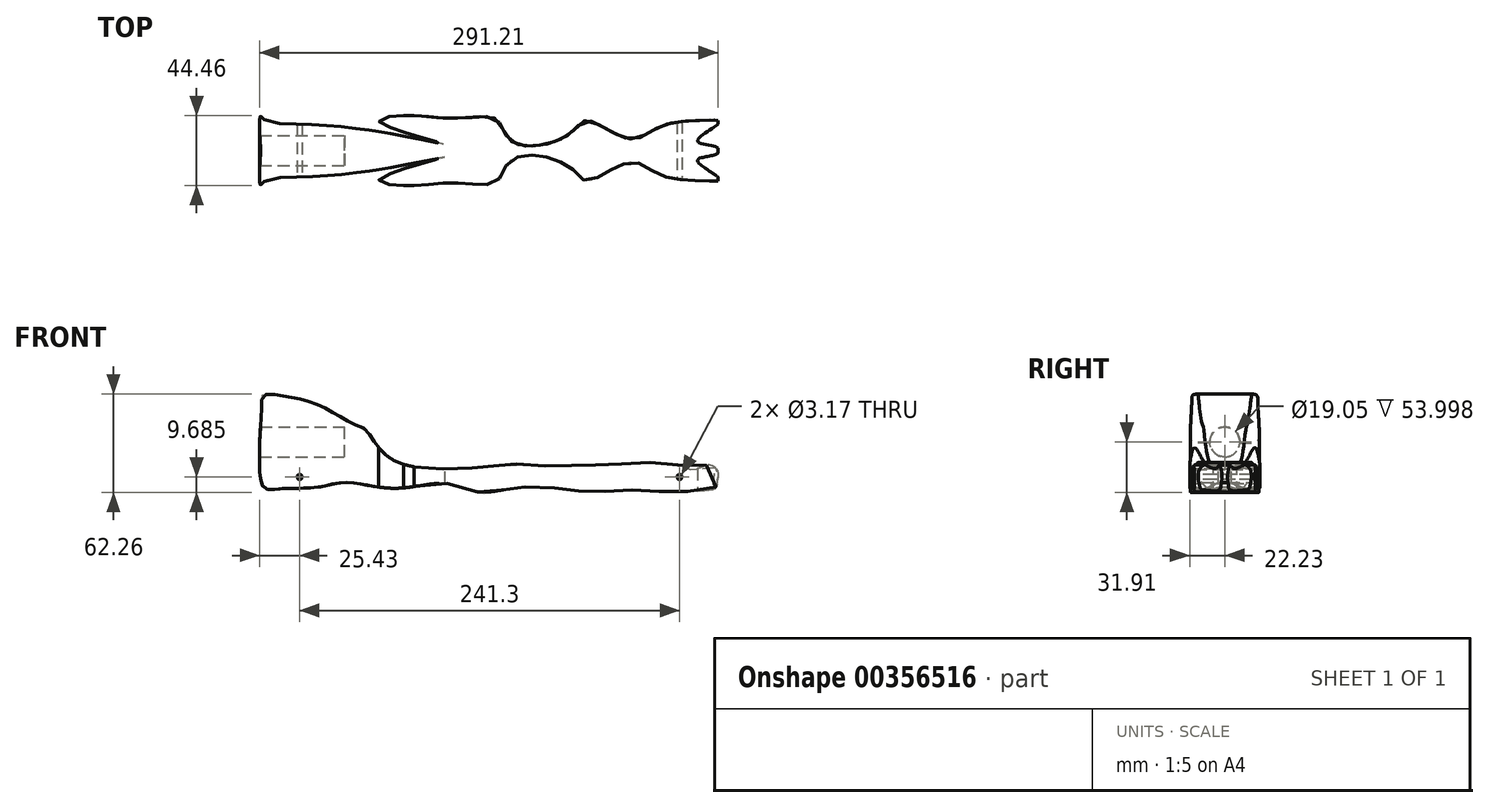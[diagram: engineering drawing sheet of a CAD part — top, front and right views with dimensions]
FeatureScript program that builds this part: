
annotation { "Feature Type Name" : "Feature", "Feature Type Description" : "" }
export const myFeature = defineFeature(function(context is Context, id is Id, definition is map)
    precondition{}
    {
        {
            var Q0;
            Q0=qCreatedBy(makeId("Front.planeOp"),FACE);
            var sketch = newSketch(context, id + "F0", { "sketchPlane" : qUnion([Q0])});
            skLineSegment(sketch, "E0.bottom", {"start": v(-146.05, 31.75) * mm, "end": v(146.05, 31.75) * mm, "construction": true});
            skLineSegment(sketch, "E0.top", {"start": v(-146.05, -31.75) * mm, "end": v(146.05, -31.75) * mm, "construction": true});
            skLineSegment(sketch, "E0.right", {"start": v(146.05, 31.75) * mm, "end": v(146.05, -31.75) * mm, "construction": true});
            skFitSpline(sketch, "E1", {"points": [v(-146.05, -17.26) * mm, v(-146.05, 0) * mm, v(-144.68, 26.37) * mm, v(-143.61, 29.95) * mm, v(-127.38, 28.65) * mm, v(-108.41, 23.36) * mm, v(-85.54, 11.1) * mm, v(-78.05, 7.16) * mm, v(-57, -13.37) * mm, v(19.02, -13.83) * mm, v(22.94, -14.7) * mm, v(96.76, -13.3) * mm, v(117.92, -14.08) * mm, v(129.64, -17.43) * mm, v(139.38, -14.69) * mm, v(144.8, -18.98) * mm, v(144.03, -27.86) * mm, v(143.14, -29.88) * mm, v(139.6, -30.43) * mm, v(115.53, -31.73) * mm, v(92.01, -30.34) * mm, v(68.34, -31.75) * mm, v(46.61, -29.95) * mm, v(18.55, -28.81) * mm, v(-6.73, -31.75) * mm, v(-27.42, -26.38) * mm, v(-60.13, -29.43) * mm, v(-91.5, -25.72) * mm, v(-108.92, -28.67) * mm, v(-133.67, -29.74) * mm, v(-143.14, -29.1) * mm, v(-146.05, -17.26) * mm]});
            skLineSegment(sketch, "E2.bottom", {"start": v(-146.05, 9.52) * mm, "end": v(-95.25, 9.52) * mm, "construction": true});
            skLineSegment(sketch, "E2.top", {"start": v(-141.83, -9.52) * mm, "end": v(-95.25, -9.52) * mm, "construction": true});
            skLineSegment(sketch, "E2.right", {"start": v(-95.25, 9.52) * mm, "end": v(-95.25, -9.52) * mm, "construction": true});
            skLineSegment(sketch, "E3", {"start": v(-146.05, 31.75) * mm, "end": v(-146.05, -31.75) * mm, "construction": true});
            skSolve(sketch);
        }
        {
            var Q0;
            Q0=qCreatedBy(makeId("Top.planeOp"),FACE);
            var sketch = newSketch(context, id + "F1", { "sketchPlane" : qUnion([Q0])});
            skLineSegment(sketch, "E4.bottom", {"start": v(-146.05, 22.22) * mm, "end": v(146.05, 22.23) * mm, "construction": true});
            skLineSegment(sketch, "E4.top", {"start": v(-146.05, -22.23) * mm, "end": v(146.05, -22.22) * mm, "construction": true});
            skLineSegment(sketch, "E4.left", {"start": v(-146.05, 22.22) * mm, "end": v(-146.05, -22.23) * mm, "construction": true});
            skLineSegment(sketch, "E4.right", {"start": v(146.05, 22.22) * mm, "end": v(146.05, -22.22) * mm, "construction": true});
            skLineSegment(sketch, "E5", {"start": v(-146.05, 0) * mm, "end": v(146.05, 0) * mm, "construction": true});
            skFitSpline(sketch, "E6", {"points": [v(-146.05, 0) * mm, v(-146.05, 19.96) * mm, v(-145.72, 21.88) * mm, v(-142.57, 19.28) * mm, v(-91.68, 14.93) * mm, v(-28.87, 4.27) * mm, v(-70.28, 18.67) * mm, v(-47.81, 22.22) * mm, v(-31.57, 20.8) * mm, v(-9.52, 21.26) * mm, v(4.85, 19.52) * mm, v(15.01, 5.2) * mm, v(50.58, 10.28) * mm, v(61.85, 19.18) * mm, v(88.92, 7.5) * mm, v(107.9, 15.13) * mm, v(134.25, 19.18) * mm, v(146.05, 17.92) * mm, v(132.12, 5.89) * mm, v(146.05, 0) * mm], "startDerivative": vector(0, 335.54) * mm, "endDerivative": vector(0, -277.49) * mm});
            skFitSpline(sketch, "E7.MirrorCS", {"points": [v(-146.05, 0) * mm, v(-146.05, -19.96) * mm, v(-145.72, -21.88) * mm, v(-142.57, -19.28) * mm, v(-91.68, -14.93) * mm, v(-28.87, -4.27) * mm, v(-70.28, -18.67) * mm, v(-47.81, -22.23) * mm, v(-31.57, -20.8) * mm, v(-9.52, -21.26) * mm, v(4.85, -19.52) * mm, v(15.01, -5.2) * mm, v(50.58, -10.28) * mm, v(61.85, -19.18) * mm, v(88.92, -7.5) * mm, v(107.9, -15.13) * mm, v(134.25, -19.18) * mm, v(146.05, -17.92) * mm, v(132.12, -5.89) * mm, v(146.05, 0) * mm], "startDerivative": vector(0, -335.54) * mm, "endDerivative": vector(0, 277.49) * mm});
            skLineSegment(sketch, "E8.MirrorCS", {"start": v(-146.05, -22.23) * mm, "end": v(146.05, -22.23) * mm});
            skSolve(sketch);
        }
        {
            var Q0;
            Q0=qCreatedBy(makeId("Right.planeOp"),FACE);
            var sketch = newSketch(context, id + "F2", { "sketchPlane" : qUnion([Q0])});
            skCircle(sketch, "E9", {"center": v(0, 0) * mm, "radius": 9.53 * mm});
            skSolve(sketch);
        }
        {
            var Q0;
            Q0=qCreatedBy(makeId("Front.planeOp"),FACE);
            var sketch = newSketch(context, id + "F3", { "sketchPlane" : qUnion([Q0])});
            skCircle(sketch, "E10", {"center": v(-120.65, -22.22) * mm, "radius": 1.59 * mm});
            skCircle(sketch, "E11", {"center": v(120.65, -22.23) * mm, "radius": 1.59 * mm});
            skSolve(sketch);
        }
        {
            var Q0;
            Q0=qSketchRegion(id+"F0",true);
            extrude(context, id + "F4", {"entities" : qUnion([Q0]), "depth" : 44.45 * mm, "symmetric" : true});
        }
        {
            var Q0;
            Q0=qSketchRegion(id+"F1",true);
            extrude(context, id + "F5", {"entities" : qUnion([Q0]), "operationType" : NewBodyOperationType.INTERSECT, "endBound" : BoundingType.THROUGH_ALL, "oppositeDirection" : true, "depth" : 60.96 * mm, "hasSecondDirection" : true, "secondDirectionBound" : BoundingType.THROUGH_ALL, "secondDirectionOppositeDirection" : false, "secondDirectionDepth" : 25.4 * mm});
        }
        {
            var Q0;
            Q0=qSketchRegion(id+"F2",true);
            extrude(context, id + "F6", {"entities" : qUnion([Q0]), "operationType" : NewBodyOperationType.REMOVE, "oppositeDirection" : true, "depth" : 152.4 * mm, "hasSecondDirection" : true, "secondDirectionOppositeDirection" : true, "secondDirectionDepth" : 92.07 * mm});
        }
        {
            var Q0;
            Q0=qSketchRegion(id+"F3",true);
            extrude(context, id + "F7", {"entities" : qUnion([Q0]), "operationType" : NewBodyOperationType.REMOVE, "oppositeDirection" : true, "depth" : 50.8 * mm, "symmetric" : true});
        }
    });
